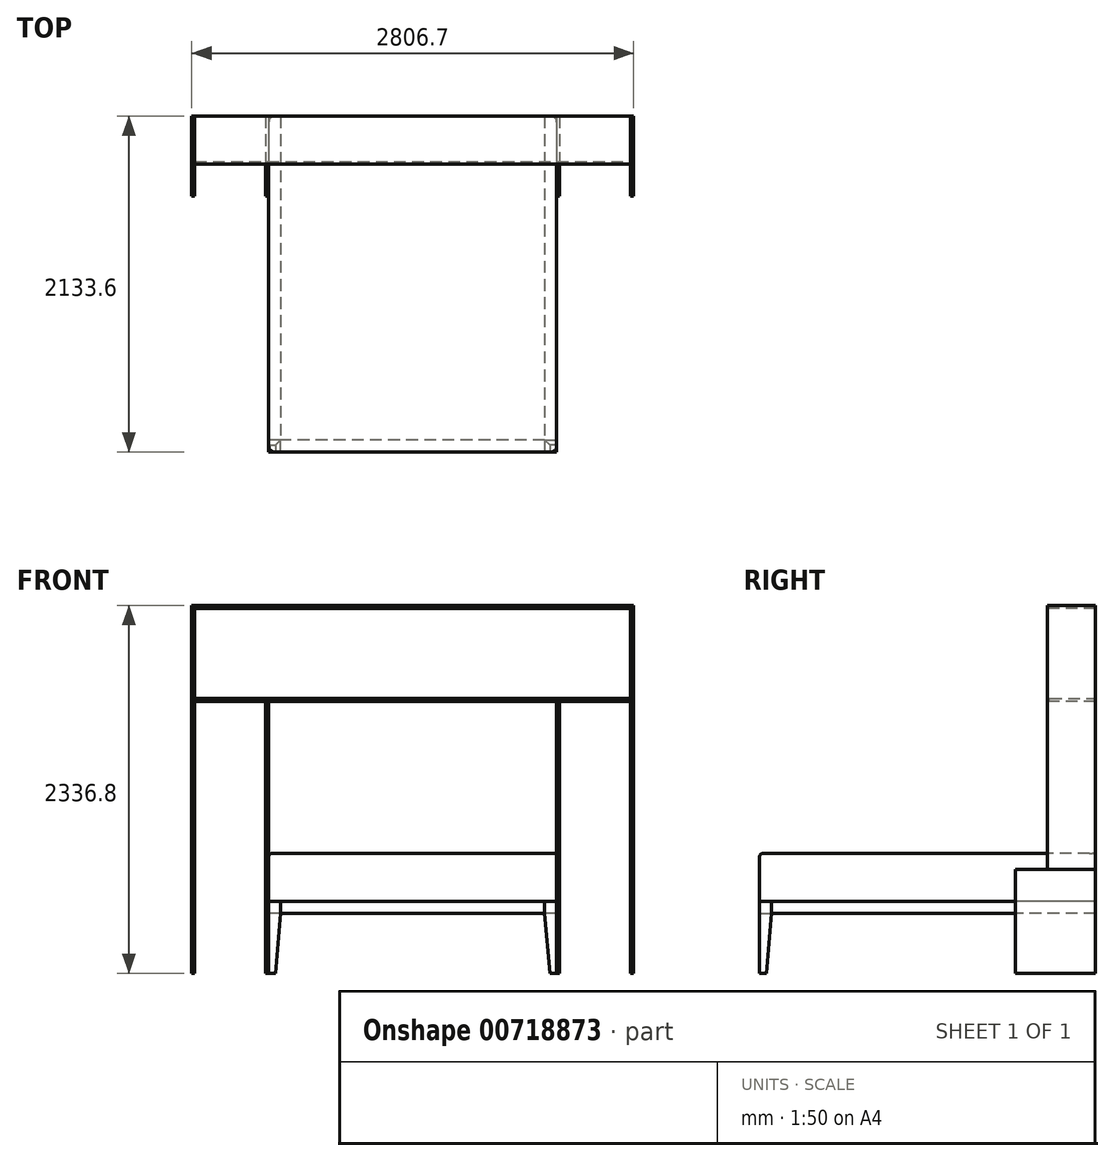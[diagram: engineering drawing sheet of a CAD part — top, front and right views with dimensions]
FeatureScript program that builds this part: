
annotation { "Feature Type Name" : "Feature", "Feature Type Description" : "" }
export const myFeature = defineFeature(function(context is Context, id is Id, definition is map)
    precondition{}
    {
        {
            var Q0;
            Q0=qCreatedBy(makeId("Top.planeOp"),FACE);
            var sketch = newSketch(context, id + "F0", { "sketchPlane" : qUnion([Q0])});
            skLineSegment(sketch, "E0.bottom", {"start": v(914.4, 1066.8) * mm, "end": v(-914.4, 1066.8) * mm});
            skLineSegment(sketch, "E0.top", {"start": v(914.4, -1066.8) * mm, "end": v(-914.4, -1066.8) * mm});
            skLineSegment(sketch, "E0.left", {"start": v(914.4, 1066.8) * mm, "end": v(914.4, -1066.8) * mm});
            skLineSegment(sketch, "E0.right", {"start": v(-914.4, 1066.8) * mm, "end": v(-914.4, -1066.8) * mm});
            skPoint(sketch, "E0.middle", {"position": v(0, 0) * mm});
            skSolve(sketch);
        }
        {
            var Q0;
            Q0=makeQuery(id+"F0.imprint","IMPRINT",FACE,{"disambiguationData":[TD([[makeQuery(id+"F0.imprint","IMPRINT",EDGE,{"derivedFrom":sQuery(id+"F0.wireOp",EDGE,"E0.bottom")}),1.0]])]});
            extrude(context, id + "F1", {"entities" : qUnion([Q0]), "depth" : 304.8 * mm, "offsetDistance" : 25.4 * mm});
        }
        {
            var Q0;
            Q0=makeQuery(id+"F1.opExtrude","SWEPT_EDGE",EDGE,{"disambiguationData":[OSD([sQuery(id+"F0.wireOp",EDGE,"E0.top"),sQuery(id+"F0.wireOp",EDGE,"E0.right")])]});
            var Q1;
            Q1=makeQuery(id+"F1.opExtrude","SWEPT_EDGE",EDGE,{"disambiguationData":[OSD([sQuery(id+"F0.wireOp",EDGE,"E0.top"),sQuery(id+"F0.wireOp",EDGE,"E0.left")])]});
            var Q2;
            Q2=makeQuery(id+"F1.opExtrude","SWEPT_EDGE",EDGE,{"disambiguationData":[OSD([sQuery(id+"F0.wireOp",EDGE,"E0.bottom"),sQuery(id+"F0.wireOp",EDGE,"E0.left")])]});
            var Q3;
            Q3=makeQuery(id+"F1.opExtrude","SWEPT_EDGE",EDGE,{"disambiguationData":[OSD([sQuery(id+"F0.wireOp",EDGE,"E0.bottom"),sQuery(id+"F0.wireOp",EDGE,"E0.right")])]});
            fillet(context, id + "F2", {"entities" : qUnion([Q0, Q1, Q2, Q3]), "radius" : 38.1 * mm, "tangentPropagation" : true, "allowEdgeOverflow" : false});
        }
        {
            var Q0;
            Q0=makeQuery(id+"F1.opExtrude","CAP_FACE",FACE,{"disambiguationData":[OSD([sQuery(id+"F0.wireOp",EDGE,"E0.bottom"),sQuery(id+"F0.wireOp",EDGE,"E0.top"),sQuery(id+"F0.wireOp",EDGE,"E0.left"),sQuery(id+"F0.wireOp",EDGE,"E0.right")])],"isStart":false});
            fillet(context, id + "F3", {"entities" : qUnion([Q0]), "radius" : 19.05 * mm, "tangentPropagation" : true, "allowEdgeOverflow" : false});
        }
        {
            var Q0;
            Q0=makeQuery(id+"F1.opExtrude","CAP_FACE",FACE,{"disambiguationData":[OSD([sQuery(id+"F0.wireOp",EDGE,"E0.bottom"),sQuery(id+"F0.wireOp",EDGE,"E0.top"),sQuery(id+"F0.wireOp",EDGE,"E0.left"),sQuery(id+"F0.wireOp",EDGE,"E0.right")])],"isStart":false});
            cPlane(context, id + "F4", {"entities" : qUnion([Q0]), "cplaneType" : CPlaneType.OFFSET, "offset" : 965.2 * mm, "width" : 152.4 * mm, "height" : 152.4 * mm});
        }
        {
            var Q0;
            Q0=makeQuery(id+"F1.opExtrude","CAP_FACE",FACE,{"disambiguationData":[OSD([sQuery(id+"F0.wireOp",EDGE,"E0.bottom"),sQuery(id+"F0.wireOp",EDGE,"E0.top"),sQuery(id+"F0.wireOp",EDGE,"E0.left"),sQuery(id+"F0.wireOp",EDGE,"E0.right")])],"isStart":true});
            var sketch = newSketch(context, id + "F5", { "sketchPlane" : qUnion([Q0])});
            skLineSegment(sketch, "E1.bottom", {"start": v(-914.4, 1066.8) * mm, "end": v(-838.2, 1066.8) * mm});
            skLineSegment(sketch, "E1.top", {"start": v(-914.4, 990.6) * mm, "end": v(-838.2, 990.6) * mm});
            skLineSegment(sketch, "E1.left", {"start": v(-914.4, 1066.8) * mm, "end": v(-914.4, 990.6) * mm});
            skLineSegment(sketch, "E1.right", {"start": v(-838.2, 1066.8) * mm, "end": v(-838.2, 990.6) * mm});
            skSolve(sketch);
        }
        {
            var Q0;
            Q0 = qSketchRegion(id + "F5", true);
            extrude(context, id + "F6", {"entities" : qUnion([Q0]), "depth" : 457.2 * mm, "offsetDistance" : 25.4 * mm});
        }
        {
            var Q0;
            Q0=makeQuery(id+"F6.opExtrude","CAP_EDGE",EDGE,{"disambiguationData":[OSD([sQuery(id+"F5.wireOp",EDGE,"E1.top")])],"isStart":false});
            var Q1;
            Q1=makeQuery(id+"F6.opExtrude","CAP_EDGE",EDGE,{"disambiguationData":[OSD([sQuery(id+"F5.wireOp",EDGE,"E1.right")])],"isStart":false});
            chamfer(context, id + "F7", {"entities" : qUnion([Q0, Q1]), "chamferType" : ChamferType.OFFSET_ANGLE, "width" : 381 * mm, "oppositeDirection" : true, "angle" : 5 * degree, "tangentPropagation" : true});
        }
        {
            var Q0;
            Q0=makeQuery(id+"F6.opExtrude","SWEPT_BODY",BODY,{"disambiguationData":[OSD([sQuery(id+"F5.wireOp",EDGE,"E1.bottom"),sQuery(id+"F5.wireOp",EDGE,"E1.top"),sQuery(id+"F5.wireOp",EDGE,"E1.left"),sQuery(id+"F5.wireOp",EDGE,"E1.right")])]});
            var Q1;
            Q1=qCreatedBy(makeId("Right.planeOp"),FACE);
            mirror(context, id + "F8", {"entities" : qUnion([Q0]), "mirrorPlane" : qUnion([Q1])});
        }
        {
            var Q0;
            Q0=makeQuery(id+"F6.opExtrude","SWEPT_FACE",FACE,{"disambiguationData":[OSD([sQuery(id+"F5.wireOp",EDGE,"E1.right")])]});
            extrude(context, id + "F9", {"entities" : qUnion([Q0]), "endBound" : BoundingType.UP_TO_NEXT, "depth" : 25.4 * mm, "offsetDistance" : 25.4 * mm});
        }
        {
            var Q0;
            Q0=makeQuery(id+"F8.opPattern","COPY",FACE,{"derivedFrom":makeQuery(id+"F6.opExtrude","SWEPT_FACE",FACE,{"disambiguationData":[OSD([sQuery(id+"F5.wireOp",EDGE,"E1.top")])]}),"instanceName":"1"});
            var Q1;
            Q1=makeQuery(id+"F6.opExtrude","SWEPT_FACE",FACE,{"disambiguationData":[OSD([sQuery(id+"F5.wireOp",EDGE,"E1.top")])]});
            var Q2;
            Q2=makeQuery(id+"F1.opExtrude","SWEPT_FACE",FACE,{"disambiguationData":[OSD([sQuery(id+"F0.wireOp",EDGE,"E0.bottom")])]});
            extrude(context, id + "F10", {"entities" : qUnion([Q0, Q1]), "endBound" : BoundingType.UP_TO_SURFACE, "depth" : 25.4 * mm, "endBoundEntityFace" : qUnion([Q2]), "offsetDistance" : 25.4 * mm});
        }
        {
            var Q0;
            {var subQ0=sQuery(id+"F5.wireOp",EDGE,"E1.left");var subQ1=sQuery(id+"F5.wireOp",EDGE,"E1.top");var subQ2=sQuery(id+"F0.wireOp",EDGE,"E0.right");Q0=makeQuery(id+"F10.opExtrude","SWEPT_FACE",FACE,{"disambiguationData":[OSD([subQ2,subQ1,subQ0]),TDD([makeQuery(id+"F8.opPattern","COPY",EDGE,{"derivedFrom":makeQuery(id+"F6.opExtrude","SWEPT_EDGE",EDGE,{"disambiguationData":[OSD([subQ2,subQ1,subQ0])]}),"instanceName":"1"})])]});}
            var sketch = newSketch(context, id + "F11", { "sketchPlane" : qUnion([Q0])});
            skPoint(sketch, "E2.0", {"position": v(-1045.37, -457.2) * mm});
            skLineSegment(sketch, "E3.bottom", {"start": v(1066.8, -457.2) * mm, "end": v(558.8, -457.2) * mm});
            skLineSegment(sketch, "E3.top", {"start": v(1066.8, 203.2) * mm, "end": v(558.8, 203.2) * mm});
            skLineSegment(sketch, "E3.left", {"start": v(1066.8, -457.2) * mm, "end": v(1066.8, 203.2) * mm});
            skLineSegment(sketch, "E3.right", {"start": v(558.8, -457.2) * mm, "end": v(558.8, 203.2) * mm});
            skSolve(sketch);
        }
        {
            var Q0;
            Q0 = qSketchRegion(id + "F11", true);
            extrude(context, id + "F12", {"entities" : qUnion([Q0]), "depth" : 19.05 * mm, "offsetDistance" : 25.4 * mm});
        }
        {
            var Q0;
            Q0=makeQuery(id+"F12.opExtrude","CAP_FACE",FACE,{"disambiguationData":[OSD([sQuery(id+"F11.wireOp",EDGE,"E3.bottom"),sQuery(id+"F11.wireOp",EDGE,"E3.top"),sQuery(id+"F11.wireOp",EDGE,"E3.left"),sQuery(id+"F11.wireOp",EDGE,"E3.right")])],"isStart":false});
            cPlane(context, id + "F13", {"entities" : qUnion([Q0]), "cplaneType" : CPlaneType.OFFSET, "offset" : 225.42 * mm, "width" : 152.4 * mm, "height" : 152.4 * mm});
        }
        {
            var Q0;
            Q0=makeQuery(id+"F12.opExtrude","SWEPT_BODY",BODY,{"disambiguationData":[OSD([sQuery(id+"F11.wireOp",EDGE,"E3.bottom"),sQuery(id+"F11.wireOp",EDGE,"E3.top"),sQuery(id+"F11.wireOp",EDGE,"E3.left"),sQuery(id+"F11.wireOp",EDGE,"E3.right")])]});
            var Q1;
            Q1=qCreatedBy(id+"F13.planeOp",FACE);
            mirror(context, id + "F14", {"entities" : qUnion([Q0]), "mirrorPlane" : qUnion([Q1])});
        }
        {
            var Q0;
            Q0=makeQuery(id+"F14.opPattern","COPY",FACE,{"derivedFrom":makeQuery(id+"F12.opExtrude","SWEPT_FACE",FACE,{"disambiguationData":[OSD([sQuery(id+"F11.wireOp",EDGE,"E3.top")])]}),"instanceName":"1"});
            var sketch = newSketch(context, id + "F15", { "sketchPlane" : qUnion([Q0])});
            skLineSegment(sketch, "E4.bottom", {"start": v(1384.3, 1066.8) * mm, "end": v(1403.35, 1066.8) * mm});
            skLineSegment(sketch, "E4.top", {"start": v(1384.3, 762) * mm, "end": v(1403.35, 762) * mm});
            skLineSegment(sketch, "E4.left", {"start": v(1384.3, 1066.8) * mm, "end": v(1384.3, 762) * mm});
            skLineSegment(sketch, "E4.right", {"start": v(1403.35, 1066.8) * mm, "end": v(1403.35, 762) * mm});
            skLineSegment(sketch, "E5.MirrorCS", {"start": v(933.45, 1066.8) * mm, "end": v(914.4, 1066.8) * mm});
            skLineSegment(sketch, "E6.MirrorCS", {"start": v(933.45, 762) * mm, "end": v(914.4, 762) * mm});
            skLineSegment(sketch, "E7.MirrorCS", {"start": v(933.45, 1066.8) * mm, "end": v(933.45, 762) * mm});
            skLineSegment(sketch, "E8.MirrorCS", {"start": v(914.4, 1066.8) * mm, "end": v(914.4, 762) * mm});
            skSolve(sketch);
        }
        {
            var Q0;
            Q0=makeQuery(id+"F15.imprint","IMPRINT",FACE,{"disambiguationData":[TD([[makeQuery(id+"F15.imprint","IMPRINT",EDGE,{"derivedFrom":sQuery(id+"F15.wireOp",EDGE,"E4.bottom")}),-1.0]])]});
            extrude(context, id + "F16", {"entities" : qUnion([Q0]), "depth" : 1676.4 * mm, "offsetDistance" : 25.4 * mm});
        }
        {
            var Q0;
            Q0=makeQuery(id+"F15.imprint","IMPRINT",FACE,{"disambiguationData":[TD([[makeQuery(id+"F15.imprint","IMPRINT",EDGE,{"derivedFrom":sQuery(id+"F15.wireOp",EDGE,"E5.MirrorCS")}),1.0]])]});
            var Q1;
            Q1=qCreatedBy(id+"F4.planeOp",FACE);
            extrude(context, id + "F17", {"entities" : qUnion([Q0]), "endBound" : BoundingType.UP_TO_SURFACE, "depth" : 25.4 * mm, "endBoundEntityFace" : qUnion([Q1]), "offsetDistance" : 25.4 * mm});
        }
        {
            var Q0;
            Q0=makeQuery(id+"F12.opExtrude","SWEPT_BODY",BODY,{"disambiguationData":[OSD([sQuery(id+"F11.wireOp",EDGE,"E3.bottom"),sQuery(id+"F11.wireOp",EDGE,"E3.top"),sQuery(id+"F11.wireOp",EDGE,"E3.left"),sQuery(id+"F11.wireOp",EDGE,"E3.right")])]});
            var Q1;
            Q1=makeQuery(id+"F16.opExtrude","SWEPT_BODY",BODY,{"disambiguationData":[OSD([sQuery(id+"F15.wireOp",EDGE,"E4.bottom"),sQuery(id+"F15.wireOp",EDGE,"E4.top"),sQuery(id+"F15.wireOp",EDGE,"E4.left"),sQuery(id+"F15.wireOp",EDGE,"E4.right")])]});
            var Q2;
            Q2=makeQuery(id+"F14.opPattern","COPY",BODY,{"derivedFrom":makeQuery(id+"F12.opExtrude","SWEPT_BODY",BODY,{"disambiguationData":[OSD([sQuery(id+"F11.wireOp",EDGE,"E3.bottom"),sQuery(id+"F11.wireOp",EDGE,"E3.top"),sQuery(id+"F11.wireOp",EDGE,"E3.left"),sQuery(id+"F11.wireOp",EDGE,"E3.right")])]}),"instanceName":"1"});
            var Q3;
            Q3=makeQuery(id+"F17.opExtrude","SWEPT_BODY",BODY,{"disambiguationData":[OSD([sQuery(id+"F15.wireOp",EDGE,"E5.MirrorCS"),sQuery(id+"F15.wireOp",EDGE,"E6.MirrorCS"),sQuery(id+"F15.wireOp",EDGE,"E7.MirrorCS"),sQuery(id+"F15.wireOp",EDGE,"E8.MirrorCS")])]});
            var Q4;
            Q4=qCreatedBy(makeId("Right.planeOp"),FACE);
            mirror(context, id + "F18", {"entities" : qUnion([Q0, Q1, Q2, Q3]), "mirrorPlane" : qUnion([Q4])});
        }
        {
            var Q0;
            Q0=makeQuery(id+"F16.opExtrude","SWEPT_FACE",FACE,{"disambiguationData":[OSD([sQuery(id+"F15.wireOp",EDGE,"E4.left")])]});
            var sketch = newSketch(context, id + "F19", { "sketchPlane" : qUnion([Q0])});
            skLineSegment(sketch, "E9.bottom", {"start": v(-1066.8, 1879.6) * mm, "end": v(-762, 1879.6) * mm});
            skLineSegment(sketch, "E9.top", {"start": v(-1066.8, 1860.55) * mm, "end": v(-762, 1860.55) * mm});
            skLineSegment(sketch, "E9.left", {"start": v(-1066.8, 1879.6) * mm, "end": v(-1066.8, 1860.55) * mm});
            skLineSegment(sketch, "E9.right", {"start": v(-762, 1879.6) * mm, "end": v(-762, 1860.55) * mm});
            skLineSegment(sketch, "E10.top", {"start": v(-771.53, 1866.9) * mm, "end": v(-768.35, 1866.9) * mm});
            skLineSegment(sketch, "E10.left", {"start": v(-771.53, 1860.55) * mm, "end": v(-771.53, 1866.9) * mm});
            skLineSegment(sketch, "E10.right", {"start": v(-768.35, 1860.55) * mm, "end": v(-768.35, 1866.9) * mm});
            skLineSegment(sketch, "E11.top", {"start": v(-777.88, 1866.9) * mm, "end": v(-774.7, 1866.9) * mm});
            skLineSegment(sketch, "E11.left", {"start": v(-777.88, 1860.55) * mm, "end": v(-777.88, 1866.9) * mm});
            skLineSegment(sketch, "E11.right", {"start": v(-774.7, 1860.55) * mm, "end": v(-774.7, 1866.9) * mm});
            skLineSegment(sketch, "E12.0", {"start": v(1028.7, 304.8) * mm, "end": v(-1028.7, 304.8) * mm});
            skLineSegment(sketch, "E13.bottom", {"start": v(-762, 1289.05) * mm, "end": v(-1066.8, 1289.05) * mm});
            skLineSegment(sketch, "E13.top", {"start": v(-762, 1270) * mm, "end": v(-1066.8, 1270) * mm});
            skLineSegment(sketch, "E13.left", {"start": v(-762, 1289.05) * mm, "end": v(-762, 1270) * mm});
            skLineSegment(sketch, "E13.right", {"start": v(-1066.8, 1289.05) * mm, "end": v(-1066.8, 1270) * mm});
            skLineSegment(sketch, "E14.top", {"start": v(-768.35, 1285.88) * mm, "end": v(-771.53, 1285.88) * mm});
            skLineSegment(sketch, "E14.left", {"start": v(-768.35, 1289.05) * mm, "end": v(-768.35, 1285.88) * mm});
            skLineSegment(sketch, "E14.right", {"start": v(-771.53, 1289.05) * mm, "end": v(-771.53, 1285.88) * mm});
            skLineSegment(sketch, "E15.top", {"start": v(-774.7, 1285.88) * mm, "end": v(-777.88, 1285.88) * mm});
            skLineSegment(sketch, "E15.left", {"start": v(-774.7, 1289.05) * mm, "end": v(-774.7, 1285.88) * mm});
            skLineSegment(sketch, "E15.right", {"start": v(-777.88, 1289.05) * mm, "end": v(-777.88, 1285.88) * mm});
            skSolve(sketch);
        }
        {
            var Q0;
            Q0=makeQuery(id+"F19.imprint","IMPRINT",FACE,{"disambiguationData":[TD([[makeQuery(id+"F19.imprint","IMPRINT",EDGE,{"derivedFrom":sQuery(id+"F19.wireOp",EDGE,"E9.bottom")}),-1.0]])]});
            var Q1;
            Q1=makeQuery(id+"F19.imprint","IMPRINT",FACE,{"disambiguationData":[TD([[makeQuery(id+"F19.imprint","IMPRINT",EDGE,{"derivedFrom":sQuery(id+"F19.wireOp",EDGE,"E13.top")}),-1.0]])]});
            extrude(context, id + "F20", {"entities" : qUnion([Q0, Q1]), "endBound" : BoundingType.UP_TO_NEXT, "depth" : 25.4 * mm, "offsetDistance" : 25.4 * mm});
        }
    });
